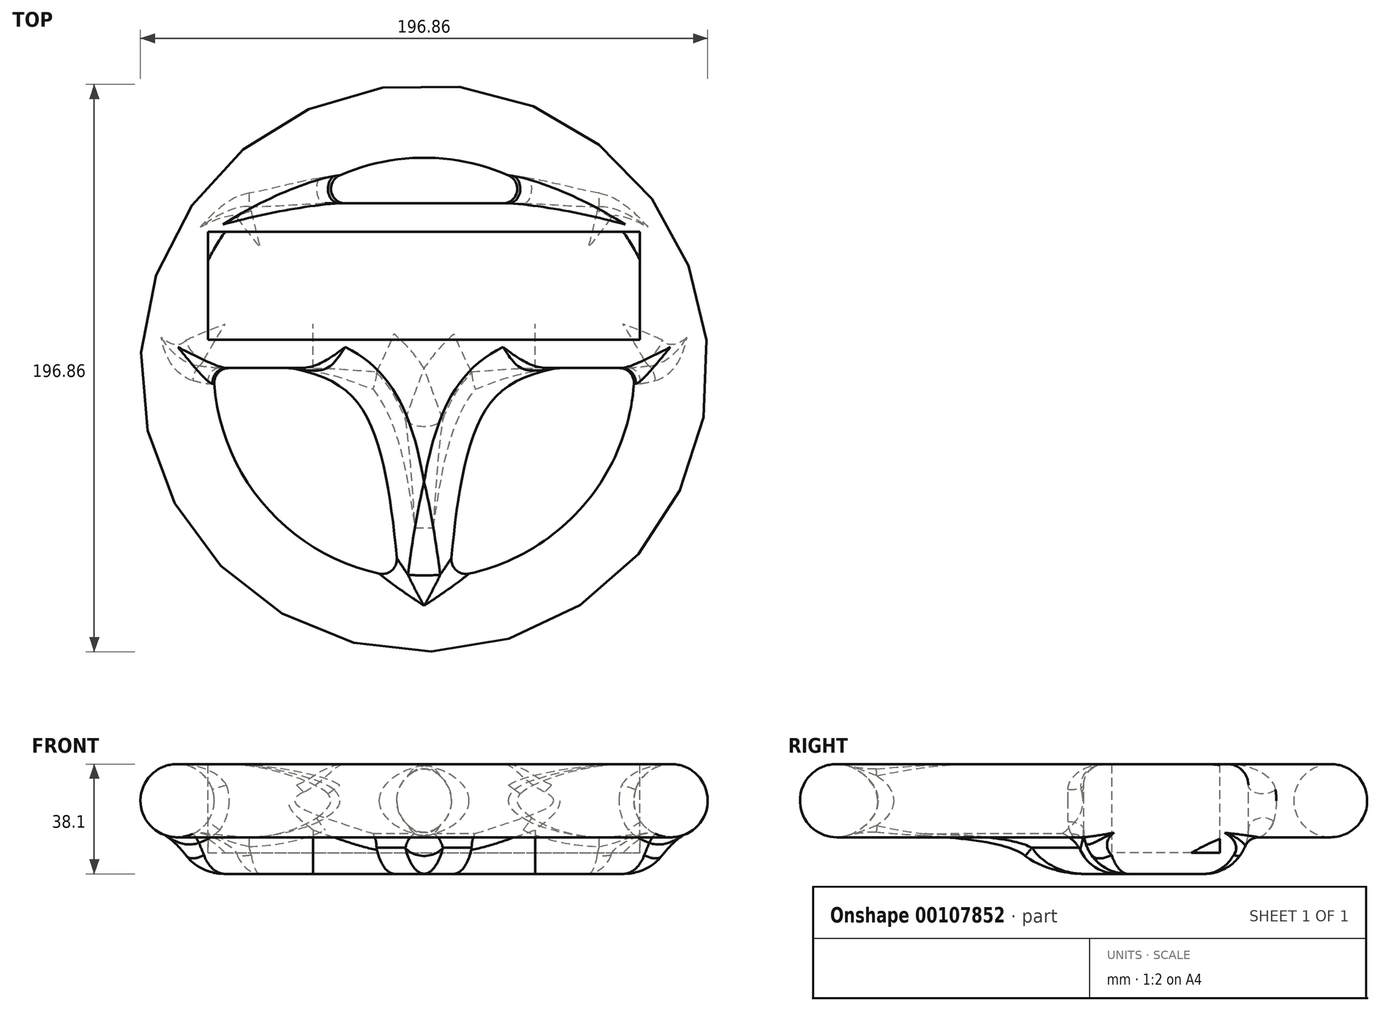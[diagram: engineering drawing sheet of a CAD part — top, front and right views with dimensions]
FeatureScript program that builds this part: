
annotation { "Feature Type Name" : "Feature", "Feature Type Description" : "" }
export const myFeature = defineFeature(function(context is Context, id is Id, definition is map)
    precondition{}
    {
        {
            var Q0;
            Q0=qCreatedBy(makeId("Top.planeOp"),FACE);
            var sketch = newSketch(context, id + "F0", { "sketchPlane" : qUnion([Q0])});
            skCircle(sketch, "E0", {"center": v(0, 0) * mm, "radius": 98.43 * mm});
            skArc(sketch, "E1", {"start": v(-73.03, 0) * mm, "mid": v(0, -73.03) * mm, "end": v(73.03, 0) * mm});
            skLineSegment(sketch, "E2", {"start": v(-45.46, 57.15) * mm, "end": v(45.46, 57.15) * mm});
            skLineSegment(sketch, "E3", {"start": v(73.03, 0) * mm, "end": v(-73.03, 0) * mm});
            skFitSpline(sketch, "E4", {"points": [v(-46.06, 0) * mm, v(-21.33, -14.47) * mm, v(-8.89, -72.48) * mm], "startDerivative": vector(87.72, -17.65) * mm, "endDerivative": vector(11.08, -128.98) * mm});
            skFitSpline(sketch, "E5.MirrorCS", {"points": [v(46.06, 0) * mm, v(21.33, -14.47) * mm, v(8.89, -72.48) * mm], "startDerivative": vector(-87.72, -17.65) * mm, "endDerivative": vector(-11.08, -128.98) * mm});
            skArc(sketch, "E6.trimOffspring", {"start": v(45.46, 57.15) * mm, "mid": v(0, 73.03) * mm, "end": v(-45.46, 57.15) * mm});
            skSolve(sketch);
        }
        {
            var Q0;
            Q0=makeQuery(id+"F0.imprint","IMPRINT",FACE,{"disambiguationData":[TD([[makeQuery(id+"F0.imprint","IMPRINT",EDGE,{"derivedFrom":sQuery(id+"F0.wireOp",EDGE,"E0")}),1.0]])]});
            var Q1;
            {var subQ0=sQuery(id+"F0.wireOp",EDGE,"E4");Q1=makeQuery(id+"F0.imprint","IMPRINT",FACE,{"disambiguationData":[TD([[makeQuery(id+"F0.imprint","IMPRINT",EDGE,{"derivedFrom":subQ0}),1.0]])]});}
            extrude(context, id + "F1", {"entities" : qUnion([Q0, Q1]), "depth" : 25.4 * mm});
        }
        {
            var Q0;
            Q0=makeQuery(id+"F1.opExtrude","CAP_EDGE",EDGE,{"disambiguationData":[OSD([sQuery(id+"F0.wireOp",EDGE,"E0")])],"isStart":false});
            var Q1;
            Q1=makeQuery(id+"F1.opExtrude","CAP_EDGE",EDGE,{"disambiguationData":[OSD([sQuery(id+"F0.wireOp",EDGE,"E0")])],"isStart":true});
            fillet(context, id + "F2", {"entities" : qUnion([Q0, Q1]), "radius" : 12.7 * mm, "tangentPropagation" : true, "allowEdgeOverflow" : false});
        }
        {
            var Q0;
            {var subQ0=sQuery(id+"F0.wireOp",EDGE,"E1");Q0=makeQuery(id+"F1.opExtrude","CAP_EDGE",EDGE,{"disambiguationData":[OSD([subQ0]),TDD([makeQuery(id+"F0.imprint","IMPRINT",EDGE,{"disambiguationData":[TD([[makeQuery(id+"F0.imprint","INTERSECT",VERTEX,{"disambiguationData":[OD(0.0)],"derivedFrom":[subQ0,sQuery(id+"F0.wireOp",EDGE,"E3")]}),-1.0]])],"derivedFrom":subQ0})])],"isStart":false});}
            var Q1;
            {var subQ0=sQuery(id+"F0.wireOp",EDGE,"E1");Q1=makeQuery(id+"F1.opExtrude","CAP_EDGE",EDGE,{"disambiguationData":[OSD([subQ0]),TDD([makeQuery(id+"F0.imprint","IMPRINT",EDGE,{"disambiguationData":[TD([[makeQuery(id+"F0.imprint","INTERSECT",VERTEX,{"disambiguationData":[OD(1.0)],"derivedFrom":[subQ0,sQuery(id+"F0.wireOp",EDGE,"E3")]}),1.0]])],"derivedFrom":subQ0})])],"isStart":false});}
            var Q2;
            Q2=makeQuery(id+"F1.opExtrude","CAP_EDGE",EDGE,{"disambiguationData":[OSD([sQuery(id+"F0.wireOp",EDGE,"E6.trimOffspring")])],"isStart":false});
            fillet(context, id + "F3", {"entities" : qUnion([Q0, Q1, Q2]), "radius" : 12.7 * mm, "tangentPropagation" : true, "allowEdgeOverflow" : false});
        }
        {
            var Q0;
            {var subQ0=sQuery(id+"F0.wireOp",EDGE,"E1");Q0=makeQuery(id+"F1.opExtrude","CAP_EDGE",EDGE,{"disambiguationData":[OSD([subQ0]),TDD([makeQuery(id+"F0.imprint","IMPRINT",EDGE,{"disambiguationData":[TD([[makeQuery(id+"F0.imprint","INTERSECT",VERTEX,{"disambiguationData":[OD(1.0)],"derivedFrom":[subQ0,sQuery(id+"F0.wireOp",EDGE,"E3")]}),1.0]])],"derivedFrom":subQ0})])],"isStart":true});}
            var Q1;
            Q1=makeQuery(id+"F1.opExtrude","CAP_EDGE",EDGE,{"disambiguationData":[OSD([sQuery(id+"F0.wireOp",EDGE,"E6.trimOffspring")])],"isStart":true});
            var Q2;
            {var subQ0=sQuery(id+"F0.wireOp",EDGE,"E1");Q2=makeQuery(id+"F1.opExtrude","CAP_EDGE",EDGE,{"disambiguationData":[OSD([subQ0]),TDD([makeQuery(id+"F0.imprint","IMPRINT",EDGE,{"disambiguationData":[TD([[makeQuery(id+"F0.imprint","INTERSECT",VERTEX,{"disambiguationData":[OD(0.0)],"derivedFrom":[subQ0,sQuery(id+"F0.wireOp",EDGE,"E3")]}),-1.0]])],"derivedFrom":subQ0})])],"isStart":true});}
            fillet(context, id + "F4", {"entities" : qUnion([Q0, Q1, Q2]), "radius" : 12.7 * mm, "tangentPropagation" : true, "allowEdgeOverflow" : false});
        }
        {
            var Q0;
            Q0=makeQuery(id+"F1.opExtrude","CAP_EDGE",EDGE,{"disambiguationData":[OSD([sQuery(id+"F0.wireOp",EDGE,"E5.MirrorCS")])],"isStart":false});
            var Q1;
            Q1=makeQuery(id+"F1.opExtrude","CAP_EDGE",EDGE,{"disambiguationData":[OSD([sQuery(id+"F0.wireOp",EDGE,"E4")])],"isStart":false});
            var Q2;
            Q2=makeQuery(id+"F1.opExtrude","CAP_EDGE",EDGE,{"disambiguationData":[OSD([sQuery(id+"F0.wireOp",EDGE,"E5.MirrorCS")])],"isStart":true});
            var Q3;
            Q3=makeQuery(id+"F1.opExtrude","CAP_EDGE",EDGE,{"disambiguationData":[OSD([sQuery(id+"F0.wireOp",EDGE,"E4")])],"isStart":true});
            fillet(context, id + "F5", {"entities" : qUnion([Q0, Q1, Q2, Q3]), "radius" : 12.7 * mm, "tangentPropagation" : true, "allowEdgeOverflow" : false});
        }
        {
            var Q0;
            {var subQ0=sQuery(id+"F0.wireOp",EDGE,"E3");Q0=makeQuery(id+"F1.opExtrude","CAP_EDGE",EDGE,{"disambiguationData":[OSD([subQ0]),TDD([makeQuery(id+"F0.imprint","IMPRINT",EDGE,{"disambiguationData":[TD([[makeQuery(id+"F0.imprint","INTERSECT",VERTEX,{"disambiguationData":[OD(1.0)],"derivedFrom":[sQuery(id+"F0.wireOp",EDGE,"E1"),subQ0]}),-1.0]])],"derivedFrom":subQ0})])],"isStart":false});}
            var Q1;
            {var subQ0=sQuery(id+"F0.wireOp",EDGE,"E3");Q1=makeQuery(id+"F1.opExtrude","CAP_EDGE",EDGE,{"disambiguationData":[OSD([subQ0]),TDD([makeQuery(id+"F0.imprint","IMPRINT",EDGE,{"disambiguationData":[TD([[makeQuery(id+"F0.imprint","INTERSECT",VERTEX,{"disambiguationData":[OD(0.0)],"derivedFrom":[sQuery(id+"F0.wireOp",EDGE,"E1"),subQ0]}),1.0]])],"derivedFrom":subQ0})])],"isStart":false});}
            var Q2;
            Q2=makeQuery(id+"F1.opExtrude","CAP_EDGE",EDGE,{"disambiguationData":[OSD([sQuery(id+"F0.wireOp",EDGE,"E2")])],"isStart":false});
            fillet(context, id + "F6", {"entities" : qUnion([Q0, Q1, Q2]), "radius" : 7.3 * mm, "tangentPropagation" : true, "allowEdgeOverflow" : false});
        }
        {
            var Q0;
            Q0=makeQuery(id+"F5.opFillet","BLEND_EDGE",EDGE,{"blendedFrom":[makeQuery(id+"F1.opExtrude","CAP_EDGE",EDGE,{"disambiguationData":[OSD([sQuery(id+"F0.wireOp",EDGE,"E5.MirrorCS")])],"isStart":false}),makeQuery(id+"F2.opFillet","BLEND_FACE",FACE,{"disambiguationData":[OSD([sQuery(id+"F0.wireOp",EDGE,"E0")])]})],"blendedInto":[makeQuery(id+"F2.opFillet","BLEND_FACE",FACE,{"disambiguationData":[OSD([sQuery(id+"F0.wireOp",EDGE,"E0")])]})]});
            var Q1;
            Q1=makeQuery(id+"F5.opFillet","BLEND_EDGE",EDGE,{"blendedFrom":[makeQuery(id+"F1.opExtrude","CAP_EDGE",EDGE,{"disambiguationData":[OSD([sQuery(id+"F0.wireOp",EDGE,"E4")])],"isStart":false}),makeQuery(id+"F2.opFillet","BLEND_FACE",FACE,{"disambiguationData":[OSD([sQuery(id+"F0.wireOp",EDGE,"E0")])]})],"blendedInto":[makeQuery(id+"F2.opFillet","BLEND_FACE",FACE,{"disambiguationData":[OSD([sQuery(id+"F0.wireOp",EDGE,"E0")])]})]});
            fillet(context, id + "F7", {"entities" : qUnion([Q0, Q1]), "radius" : 5.08 * mm, "tangentPropagation" : true, "allowEdgeOverflow" : false});
        }
        {
            var Q0;
            Q0=makeQuery(id+"F1.opExtrude","CAP_FACE",FACE,{"disambiguationData":[OSD([sQuery(id+"F0.wireOp",EDGE,"E0"),sQuery(id+"F0.wireOp",EDGE,"E1"),sQuery(id+"F0.wireOp",EDGE,"E2"),sQuery(id+"F0.wireOp",EDGE,"E3"),sQuery(id+"F0.wireOp",EDGE,"E4"),sQuery(id+"F0.wireOp",EDGE,"E5.MirrorCS"),sQuery(id+"F0.wireOp",EDGE,"E6.trimOffspring")])],"isStart":true});
            extrude(context, id + "F8", {"entities" : qUnion([Q0]), "operationType" : NewBodyOperationType.ADD, "depth" : 12.7 * mm});
        }
        {
            var Q0;
            {var subQ0=sQuery(id+"F0.wireOp",EDGE,"E6.trimOffspring");var subQ1=sQuery(id+"F0.wireOp",EDGE,"E5.MirrorCS");var subQ2=sQuery(id+"F0.wireOp",EDGE,"E4");var subQ3=sQuery(id+"F0.wireOp",EDGE,"E3");var subQ4=sQuery(id+"F0.wireOp",EDGE,"E2");var subQ5=sQuery(id+"F0.wireOp",EDGE,"E1");var subQ6=sQuery(id+"F0.wireOp",EDGE,"E0");var subQ7=makeQuery(id+"F5.opFillet","BLEND_EDGE",EDGE,{"blendedFrom":[makeQuery(id+"F1.opExtrude","CAP_EDGE",EDGE,{"disambiguationData":[OSD([subQ2])],"isStart":true}),makeQuery(id+"F1.opExtrude","CAP_FACE",FACE,{"disambiguationData":[OSD([subQ6,subQ5,subQ4,subQ3,subQ2,subQ1,subQ0])],"isStart":true})],"blendedInto":[makeQuery(id+"F1.opExtrude","CAP_FACE",FACE,{"disambiguationData":[OSD([subQ6,subQ5,subQ4,subQ3,subQ2,subQ1,subQ0])],"isStart":true})]});Q0=makeQuery(id+"F8.boolean.opBoolean","MERGE",EDGE,{"derivedFrom":[subQ7,makeQuery(id+"F8.opExtrude","CAP_EDGE",EDGE,{"disambiguationData":[OSD([subQ6,subQ5,subQ4,subQ3,subQ2,subQ1,subQ0]),TDD([subQ7])],"isStart":true})]});}
            var Q1;
            {var subQ0=sQuery(id+"F0.wireOp",EDGE,"E6.trimOffspring");var subQ1=sQuery(id+"F0.wireOp",EDGE,"E5.MirrorCS");var subQ2=sQuery(id+"F0.wireOp",EDGE,"E4");var subQ3=sQuery(id+"F0.wireOp",EDGE,"E3");var subQ4=sQuery(id+"F0.wireOp",EDGE,"E2");var subQ5=sQuery(id+"F0.wireOp",EDGE,"E1");var subQ6=sQuery(id+"F0.wireOp",EDGE,"E0");var subQ7=makeQuery(id+"F5.opFillet","BLEND_EDGE",EDGE,{"blendedFrom":[makeQuery(id+"F1.opExtrude","CAP_EDGE",EDGE,{"disambiguationData":[OSD([subQ1])],"isStart":true}),makeQuery(id+"F1.opExtrude","CAP_FACE",FACE,{"disambiguationData":[OSD([subQ6,subQ5,subQ4,subQ3,subQ2,subQ1,subQ0])],"isStart":true})],"blendedInto":[makeQuery(id+"F1.opExtrude","CAP_FACE",FACE,{"disambiguationData":[OSD([subQ6,subQ5,subQ4,subQ3,subQ2,subQ1,subQ0])],"isStart":true})]});Q1=makeQuery(id+"F8.boolean.opBoolean","MERGE",EDGE,{"derivedFrom":[subQ7,makeQuery(id+"F8.opExtrude","CAP_EDGE",EDGE,{"disambiguationData":[OSD([subQ6,subQ5,subQ4,subQ3,subQ2,subQ1,subQ0]),TDD([subQ7])],"isStart":true})]});}
            var Q2;
            {var subQ0=sQuery(id+"F0.wireOp",EDGE,"E3");var subQ1=sQuery(id+"F0.wireOp",EDGE,"E5.MirrorCS");Q2=makeQuery(id+"F5.opFillet","BLEND_EDGE",EDGE,{"blendedFrom":[makeQuery(id+"F1.opExtrude","CAP_EDGE",EDGE,{"disambiguationData":[OSD([subQ1])],"isStart":true}),makeQuery(id+"F1.opExtrude","SWEPT_FACE",FACE,{"disambiguationData":[OSD([subQ0]),TDD([makeQuery(id+"F0.imprint","IMPRINT",EDGE,{"disambiguationData":[TD([[makeQuery(id+"F0.imprint","INTERSECT",VERTEX,{"disambiguationData":[OD(1.0)],"derivedFrom":[sQuery(id+"F0.wireOp",EDGE,"E1"),subQ0]}),-1.0]])],"derivedFrom":subQ0})])]})],"blendedInto":[makeQuery(id+"F1.opExtrude","SWEPT_FACE",FACE,{"disambiguationData":[OSD([subQ0]),TDD([makeQuery(id+"F0.imprint","IMPRINT",EDGE,{"disambiguationData":[TD([[makeQuery(id+"F0.imprint","INTERSECT",VERTEX,{"disambiguationData":[OD(1.0)],"derivedFrom":[sQuery(id+"F0.wireOp",EDGE,"E1"),subQ0]}),-1.0]])],"derivedFrom":subQ0})])]})]});}
            var Q3;
            {var subQ0=sQuery(id+"F0.wireOp",EDGE,"E3");var subQ1=sQuery(id+"F0.wireOp",EDGE,"E4");Q3=makeQuery(id+"F5.opFillet","BLEND_EDGE",EDGE,{"blendedFrom":[makeQuery(id+"F1.opExtrude","CAP_EDGE",EDGE,{"disambiguationData":[OSD([subQ1])],"isStart":true}),makeQuery(id+"F1.opExtrude","SWEPT_FACE",FACE,{"disambiguationData":[OSD([subQ0]),TDD([makeQuery(id+"F0.imprint","IMPRINT",EDGE,{"disambiguationData":[TD([[makeQuery(id+"F0.imprint","INTERSECT",VERTEX,{"disambiguationData":[OD(0.0)],"derivedFrom":[sQuery(id+"F0.wireOp",EDGE,"E1"),subQ0]}),1.0]])],"derivedFrom":subQ0})])]})],"blendedInto":[makeQuery(id+"F1.opExtrude","SWEPT_FACE",FACE,{"disambiguationData":[OSD([subQ0]),TDD([makeQuery(id+"F0.imprint","IMPRINT",EDGE,{"disambiguationData":[TD([[makeQuery(id+"F0.imprint","INTERSECT",VERTEX,{"disambiguationData":[OD(0.0)],"derivedFrom":[sQuery(id+"F0.wireOp",EDGE,"E1"),subQ0]}),1.0]])],"derivedFrom":subQ0})])]})]});}
            fillet(context, id + "F9", {"entities" : qUnion([Q0, Q1, Q2, Q3]), "radius" : 10.16 * mm, "tangentPropagation" : true, "allowEdgeOverflow" : false});
        }
        {
            var Q0;
            Q0=makeQuery(id+"F8.opExtrude","CAP_FACE",FACE,{"disambiguationData":[OSD([sQuery(id+"F0.wireOp",EDGE,"E0"),sQuery(id+"F0.wireOp",EDGE,"E1"),sQuery(id+"F0.wireOp",EDGE,"E2"),sQuery(id+"F0.wireOp",EDGE,"E3"),sQuery(id+"F0.wireOp",EDGE,"E4"),sQuery(id+"F0.wireOp",EDGE,"E5.MirrorCS"),sQuery(id+"F0.wireOp",EDGE,"E6.trimOffspring")])],"isStart":false});
            fillet(context, id + "F10", {"entities" : qUnion([Q0]), "radius" : 15.24 * mm, "tangentPropagation" : true, "allowEdgeOverflow" : false});
        }
        {
            var Q0;
            {var subQ0=sQuery(id+"F0.wireOp",EDGE,"E0");var subQ1=sQuery(id+"F0.wireOp",EDGE,"E6.trimOffspring");var subQ2=sQuery(id+"F0.wireOp",EDGE,"E5.MirrorCS");var subQ3=sQuery(id+"F0.wireOp",EDGE,"E4");var subQ4=sQuery(id+"F0.wireOp",EDGE,"E3");var subQ5=sQuery(id+"F0.wireOp",EDGE,"E2");var subQ6=sQuery(id+"F0.wireOp",EDGE,"E1");Q0=makeQuery(id+"F10.opFillet","BLEND_EDGE",EDGE,{"blendedFrom":[makeQuery(id+"F8.opExtrude","CAP_EDGE",EDGE,{"disambiguationData":[OSD([subQ0,subQ6,subQ5,subQ4,subQ3,subQ2,subQ1]),TDD([makeQuery(id+"F2.opFillet","BLEND_EDGE",EDGE,{"blendedFrom":[makeQuery(id+"F1.opExtrude","CAP_EDGE",EDGE,{"disambiguationData":[OSD([subQ0])],"isStart":true}),makeQuery(id+"F1.opExtrude","CAP_FACE",FACE,{"disambiguationData":[OSD([subQ0,subQ6,subQ5,subQ4,subQ3,subQ2,subQ1])],"isStart":true})],"blendedInto":[makeQuery(id+"F1.opExtrude","CAP_FACE",FACE,{"disambiguationData":[OSD([subQ0,subQ6,subQ5,subQ4,subQ3,subQ2,subQ1])],"isStart":true})]})])],"isStart":false}),makeQuery(id+"F2.opFillet","BLEND_FACE",FACE,{"disambiguationData":[OSD([subQ0])]})],"blendedInto":[makeQuery(id+"F2.opFillet","BLEND_FACE",FACE,{"disambiguationData":[OSD([subQ0])]})]});}
            fillet(context, id + "F11", {"entities" : qUnion([Q0]), "radius" : 25.4 * mm, "tangentPropagation" : true, "allowEdgeOverflow" : false});
        }
        {
            var Q0;
            {var subQ0=sQuery(id+"F0.wireOp",EDGE,"E3");var subQ1=sQuery(id+"F0.wireOp",EDGE,"E1");var subQ2=sQuery(id+"F0.wireOp",EDGE,"E5.MirrorCS");var subQ3=sQuery(id+"F0.wireOp",EDGE,"E6.trimOffspring");var subQ4=sQuery(id+"F0.wireOp",EDGE,"E4");var subQ5=sQuery(id+"F0.wireOp",EDGE,"E2");var subQ6=sQuery(id+"F0.wireOp",EDGE,"E0");Q0=makeQuery(id+"F10.opFillet","BLEND_EDGE",EDGE,{"blendedFrom":[makeQuery(id+"F8.opExtrude","CAP_EDGE",EDGE,{"disambiguationData":[OSD([subQ6,subQ1,subQ5,subQ0,subQ4,subQ2,subQ3]),TDD([makeQuery(id+"F2.opFillet","BLEND_EDGE",EDGE,{"blendedFrom":[makeQuery(id+"F1.opExtrude","CAP_EDGE",EDGE,{"disambiguationData":[OSD([subQ6])],"isStart":true}),makeQuery(id+"F1.opExtrude","CAP_FACE",FACE,{"disambiguationData":[OSD([subQ6,subQ1,subQ5,subQ0,subQ4,subQ2,subQ3])],"isStart":true})],"blendedInto":[makeQuery(id+"F1.opExtrude","CAP_FACE",FACE,{"disambiguationData":[OSD([subQ6,subQ1,subQ5,subQ0,subQ4,subQ2,subQ3])],"isStart":true})]})])],"isStart":false}),makeQuery(id+"F8.opExtrude","CAP_EDGE",EDGE,{"disambiguationData":[OSD([subQ0]),TDD([makeQuery(id+"F1.opExtrude","CAP_EDGE",EDGE,{"disambiguationData":[OSD([subQ0]),TDD([makeQuery(id+"F0.imprint","IMPRINT",EDGE,{"disambiguationData":[TD([[makeQuery(id+"F0.imprint","INTERSECT",VERTEX,{"disambiguationData":[OD(1.0)],"derivedFrom":[subQ1,subQ0]}),-1.0]])],"derivedFrom":subQ0})])],"isStart":true})])],"isStart":false})],"blendedInto":[]});}
            var Q1;
            {var subQ0=sQuery(id+"F0.wireOp",EDGE,"E6.trimOffspring");var subQ1=sQuery(id+"F0.wireOp",EDGE,"E5.MirrorCS");var subQ2=sQuery(id+"F0.wireOp",EDGE,"E4");var subQ3=sQuery(id+"F0.wireOp",EDGE,"E3");var subQ4=sQuery(id+"F0.wireOp",EDGE,"E2");var subQ5=sQuery(id+"F0.wireOp",EDGE,"E1");var subQ6=sQuery(id+"F0.wireOp",EDGE,"E0");Q1=makeQuery(id+"F10.opFillet","BLEND_EDGE",EDGE,{"blendedFrom":[makeQuery(id+"F8.opExtrude","CAP_EDGE",EDGE,{"disambiguationData":[OSD([subQ4])],"isStart":false}),makeQuery(id+"F8.opExtrude","CAP_EDGE",EDGE,{"disambiguationData":[OSD([subQ6,subQ5,subQ4,subQ3,subQ2,subQ1,subQ0]),TDD([makeQuery(id+"F2.opFillet","BLEND_EDGE",EDGE,{"blendedFrom":[makeQuery(id+"F1.opExtrude","CAP_EDGE",EDGE,{"disambiguationData":[OSD([subQ6])],"isStart":true}),makeQuery(id+"F1.opExtrude","CAP_FACE",FACE,{"disambiguationData":[OSD([subQ6,subQ5,subQ4,subQ3,subQ2,subQ1,subQ0])],"isStart":true})],"blendedInto":[makeQuery(id+"F1.opExtrude","CAP_FACE",FACE,{"disambiguationData":[OSD([subQ6,subQ5,subQ4,subQ3,subQ2,subQ1,subQ0])],"isStart":true})]})])],"isStart":false})],"blendedInto":[]});}
            var Q2;
            {var subQ0=sQuery(id+"F0.wireOp",EDGE,"E3");var subQ1=sQuery(id+"F0.wireOp",EDGE,"E1");var subQ2=sQuery(id+"F0.wireOp",EDGE,"E4");var subQ3=sQuery(id+"F0.wireOp",EDGE,"E0");var subQ4=sQuery(id+"F0.wireOp",EDGE,"E6.trimOffspring");var subQ5=sQuery(id+"F0.wireOp",EDGE,"E5.MirrorCS");var subQ6=sQuery(id+"F0.wireOp",EDGE,"E2");Q2=makeQuery(id+"F11.opFillet","BLEND_EDGE",EDGE,{"blendedFrom":[makeQuery(id+"F10.opFillet","BLEND_EDGE",EDGE,{"blendedFrom":[makeQuery(id+"F8.opExtrude","CAP_EDGE",EDGE,{"disambiguationData":[OSD([subQ3,subQ1,subQ6,subQ0,subQ2,subQ5,subQ4]),TDD([makeQuery(id+"F2.opFillet","BLEND_EDGE",EDGE,{"blendedFrom":[makeQuery(id+"F1.opExtrude","CAP_EDGE",EDGE,{"disambiguationData":[OSD([subQ3])],"isStart":true}),makeQuery(id+"F1.opExtrude","CAP_FACE",FACE,{"disambiguationData":[OSD([subQ3,subQ1,subQ6,subQ0,subQ2,subQ5,subQ4])],"isStart":true})],"blendedInto":[makeQuery(id+"F1.opExtrude","CAP_FACE",FACE,{"disambiguationData":[OSD([subQ3,subQ1,subQ6,subQ0,subQ2,subQ5,subQ4])],"isStart":true})]})])],"isStart":false}),makeQuery(id+"F2.opFillet","BLEND_FACE",FACE,{"disambiguationData":[OSD([subQ3])]})],"blendedInto":[makeQuery(id+"F2.opFillet","BLEND_FACE",FACE,{"disambiguationData":[OSD([subQ3])]})]}),makeQuery(id+"F10.opFillet","BLEND_FACE",FACE,{"disambiguationData":[OSD([subQ0]),TDD([makeQuery(id+"F8.opExtrude","CAP_EDGE",EDGE,{"disambiguationData":[OSD([subQ0]),TDD([makeQuery(id+"F1.opExtrude","CAP_EDGE",EDGE,{"disambiguationData":[OSD([subQ0]),TDD([makeQuery(id+"F0.imprint","IMPRINT",EDGE,{"disambiguationData":[TD([[makeQuery(id+"F0.imprint","INTERSECT",VERTEX,{"disambiguationData":[OD(0.0)],"derivedFrom":[subQ1,subQ0]}),1.0]])],"derivedFrom":subQ0})])],"isStart":true})])],"isStart":false})]),OD(0.0)]})],"blendedInto":[makeQuery(id+"F10.opFillet","BLEND_FACE",FACE,{"disambiguationData":[OSD([subQ0]),TDD([makeQuery(id+"F8.opExtrude","CAP_EDGE",EDGE,{"disambiguationData":[OSD([subQ0]),TDD([makeQuery(id+"F1.opExtrude","CAP_EDGE",EDGE,{"disambiguationData":[OSD([subQ0]),TDD([makeQuery(id+"F0.imprint","IMPRINT",EDGE,{"disambiguationData":[TD([[makeQuery(id+"F0.imprint","INTERSECT",VERTEX,{"disambiguationData":[OD(0.0)],"derivedFrom":[subQ1,subQ0]}),1.0]])],"derivedFrom":subQ0})])],"isStart":true})])],"isStart":false})]),OD(0.0)]})]});}
            fillet(context, id + "F12", {"entities" : qUnion([Q0, Q1, Q2]), "radius" : 7.62 * mm, "tangentPropagation" : true, "allowEdgeOverflow" : false});
        }
        {
            var Q0;
            {var subQ0=sQuery(id+"F0.wireOp",EDGE,"E6.trimOffspring");var subQ1=sQuery(id+"F0.wireOp",EDGE,"E5.MirrorCS");var subQ2=sQuery(id+"F0.wireOp",EDGE,"E4");var subQ3=sQuery(id+"F0.wireOp",EDGE,"E3");var subQ4=sQuery(id+"F0.wireOp",EDGE,"E2");var subQ5=sQuery(id+"F0.wireOp",EDGE,"E1");var subQ6=sQuery(id+"F0.wireOp",EDGE,"E0");var subQ7=makeQuery(id+"F1.opExtrude","CAP_FACE",FACE,{"disambiguationData":[OSD([subQ6,subQ5,subQ4,subQ3,subQ2,subQ1,subQ0])],"isStart":true});Q0=makeQuery(id+"F10.opFillet","BLEND_EDGE",EDGE,{"blendedFrom":[makeQuery(id+"F8.opExtrude","CAP_EDGE",EDGE,{"disambiguationData":[OSD([subQ6,subQ5,subQ4,subQ3,subQ2,subQ1,subQ0]),TDD([makeQuery(id+"F5.opFillet","BLEND_EDGE",EDGE,{"blendedFrom":[makeQuery(id+"F1.opExtrude","CAP_EDGE",EDGE,{"disambiguationData":[OSD([subQ2])],"isStart":true}),subQ7],"blendedInto":[subQ7]})])],"isStart":false}),makeQuery(id+"F8.opExtrude","CAP_EDGE",EDGE,{"disambiguationData":[OSD([subQ6,subQ5,subQ4,subQ3,subQ2,subQ1,subQ0]),TDD([makeQuery(id+"F5.opFillet","BLEND_EDGE",EDGE,{"blendedFrom":[makeQuery(id+"F1.opExtrude","CAP_EDGE",EDGE,{"disambiguationData":[OSD([subQ1])],"isStart":true}),subQ7],"blendedInto":[subQ7]})])],"isStart":false})],"blendedInto":[]});}
            fillet(context, id + "F13", {"entities" : qUnion([Q0]), "radius" : 7.62 * mm, "tangentPropagation" : true, "allowEdgeOverflow" : false});
        }
        {
            var Q0;
            Q0=makeQuery(id+"F6.opFillet","BLEND_EDGE",EDGE,{"disambiguationData":[OD(1.0)],"blendedFrom":[makeQuery(id+"F1.opExtrude","CAP_EDGE",EDGE,{"disambiguationData":[OSD([sQuery(id+"F0.wireOp",EDGE,"E2")])],"isStart":false}),makeQuery(id+"F2.opFillet","BLEND_FACE",FACE,{"disambiguationData":[OSD([sQuery(id+"F0.wireOp",EDGE,"E0")])]})],"blendedInto":[makeQuery(id+"F2.opFillet","BLEND_FACE",FACE,{"disambiguationData":[OSD([sQuery(id+"F0.wireOp",EDGE,"E0")])]})]});
            var Q1;
            {var subQ0=sQuery(id+"F0.wireOp",EDGE,"E3");Q1=makeQuery(id+"F6.opFillet","BLEND_EDGE",EDGE,{"blendedFrom":[makeQuery(id+"F1.opExtrude","CAP_EDGE",EDGE,{"disambiguationData":[OSD([subQ0]),TDD([makeQuery(id+"F0.imprint","IMPRINT",EDGE,{"disambiguationData":[TD([[makeQuery(id+"F0.imprint","INTERSECT",VERTEX,{"disambiguationData":[OD(0.0)],"derivedFrom":[sQuery(id+"F0.wireOp",EDGE,"E1"),subQ0]}),1.0]])],"derivedFrom":subQ0})])],"isStart":false}),makeQuery(id+"F2.opFillet","BLEND_FACE",FACE,{"disambiguationData":[OSD([sQuery(id+"F0.wireOp",EDGE,"E0")])]})],"blendedInto":[makeQuery(id+"F2.opFillet","BLEND_FACE",FACE,{"disambiguationData":[OSD([sQuery(id+"F0.wireOp",EDGE,"E0")])]})]});}
            var Q2;
            {var subQ0=sQuery(id+"F0.wireOp",EDGE,"E3");Q2=makeQuery(id+"F6.opFillet","BLEND_EDGE",EDGE,{"blendedFrom":[makeQuery(id+"F1.opExtrude","CAP_EDGE",EDGE,{"disambiguationData":[OSD([subQ0]),TDD([makeQuery(id+"F0.imprint","IMPRINT",EDGE,{"disambiguationData":[TD([[makeQuery(id+"F0.imprint","INTERSECT",VERTEX,{"disambiguationData":[OD(1.0)],"derivedFrom":[sQuery(id+"F0.wireOp",EDGE,"E1"),subQ0]}),-1.0]])],"derivedFrom":subQ0})])],"isStart":false}),makeQuery(id+"F2.opFillet","BLEND_FACE",FACE,{"disambiguationData":[OSD([sQuery(id+"F0.wireOp",EDGE,"E0")])]})],"blendedInto":[makeQuery(id+"F2.opFillet","BLEND_FACE",FACE,{"disambiguationData":[OSD([sQuery(id+"F0.wireOp",EDGE,"E0")])]})]});}
            var Q3;
            Q3=makeQuery(id+"F6.opFillet","BLEND_EDGE",EDGE,{"disambiguationData":[OD(0.0)],"blendedFrom":[makeQuery(id+"F1.opExtrude","CAP_EDGE",EDGE,{"disambiguationData":[OSD([sQuery(id+"F0.wireOp",EDGE,"E2")])],"isStart":false}),makeQuery(id+"F2.opFillet","BLEND_FACE",FACE,{"disambiguationData":[OSD([sQuery(id+"F0.wireOp",EDGE,"E0")])]})],"blendedInto":[makeQuery(id+"F2.opFillet","BLEND_FACE",FACE,{"disambiguationData":[OSD([sQuery(id+"F0.wireOp",EDGE,"E0")])]})]});
            fillet(context, id + "F14", {"entities" : qUnion([Q0, Q1, Q2, Q3]), "radius" : 5.08 * mm, "tangentPropagation" : true, "allowEdgeOverflow" : false});
        }
        {
            var Q0;
            Q0=makeQuery(id+"F5.opFillet","BLEND_EDGE",EDGE,{"blendedFrom":[makeQuery(id+"F1.opExtrude","CAP_EDGE",EDGE,{"disambiguationData":[OSD([sQuery(id+"F0.wireOp",EDGE,"E4")])],"isStart":false}),makeQuery(id+"F1.opExtrude","CAP_EDGE",EDGE,{"disambiguationData":[OSD([sQuery(id+"F0.wireOp",EDGE,"E5.MirrorCS")])],"isStart":false})],"blendedInto":[]});
            fillet(context, id + "F15", {"entities" : qUnion([Q0]), "radius" : 7.62 * mm, "tangentPropagation" : true, "allowEdgeOverflow" : false});
        }
        {
            var Q0;
            Q0=makeQuery(id+"F1.opExtrude","CAP_FACE",FACE,{"disambiguationData":[OSD([sQuery(id+"F0.wireOp",EDGE,"E0"),sQuery(id+"F0.wireOp",EDGE,"E1"),sQuery(id+"F0.wireOp",EDGE,"E2"),sQuery(id+"F0.wireOp",EDGE,"E3"),sQuery(id+"F0.wireOp",EDGE,"E4"),sQuery(id+"F0.wireOp",EDGE,"E5.MirrorCS"),sQuery(id+"F0.wireOp",EDGE,"E6.trimOffspring")])],"isStart":false});
            var sketch = newSketch(context, id + "F16", { "sketchPlane" : qUnion([Q0])});
            skLineSegment(sketch, "E7.bottom", {"start": v(-74.93, 47.3) * mm, "end": v(74.93, 47.3) * mm});
            skLineSegment(sketch, "E7.top", {"start": v(-74.93, 9.84) * mm, "end": v(74.93, 9.84) * mm});
            skLineSegment(sketch, "E7.left", {"start": v(-74.93, 47.3) * mm, "end": v(-74.93, 9.84) * mm});
            skLineSegment(sketch, "E7.right", {"start": v(74.93, 47.3) * mm, "end": v(74.93, 9.84) * mm});
            skSolve(sketch);
        }
        {
            var Q0;
            {var subQ1=sQuery(id+"F16.wireOp",EDGE,"E7.top");Q0=makeQuery(id+"F16.imprint","IMPRINT",FACE,{"disambiguationData":[TD([[makeQuery(id+"F16.imprint","IMPRINT",EDGE,{"derivedFrom":subQ1}),1.0]])]});}
            var Q1;
            {var subQ0=sQuery(id+"F16.wireOp",EDGE,"E7.left");var subQ1=sQuery(id+"F16.wireOp",EDGE,"E7.bottom");var subQ2=makeQuery(id+"F16.imprint","INTERSECT",VERTEX,{"derivedFrom":[subQ1,subQ0]});Q1=makeQuery(id+"F16.imprint","IMPRINT",FACE,{"disambiguationData":[TD([[makeQuery(id+"F16.imprint","IMPRINT",EDGE,{"disambiguationData":[TD([[subQ2,-1.0]])],"derivedFrom":subQ1}),-1.0]])]});}
            var Q2;
            {var subQ0=sQuery(id+"F16.wireOp",EDGE,"E7.right");var subQ1=sQuery(id+"F16.wireOp",EDGE,"E7.bottom");var subQ2=makeQuery(id+"F16.imprint","INTERSECT",VERTEX,{"derivedFrom":[subQ1,subQ0]});Q2=makeQuery(id+"F16.imprint","IMPRINT",FACE,{"disambiguationData":[TD([[makeQuery(id+"F16.imprint","IMPRINT",EDGE,{"disambiguationData":[TD([[subQ2,1.0]])],"derivedFrom":subQ1}),-1.0]])]});}
            extrude(context, id + "F17", {"entities" : qUnion([Q0, Q1, Q2]), "operationType" : NewBodyOperationType.REMOVE, "oppositeDirection" : true, "depth" : 25.4 * mm});
        }
        {
            var Q0;
            Q0=makeQuery(id+"F17.boolean.opBoolean","COPY",FACE,{"derivedFrom":makeQuery(id+"F17.opExtrude","CAP_FACE",FACE,{"disambiguationData":[OSD([sQuery(id+"F16.wireOp",EDGE,"E7.bottom"),sQuery(id+"F16.wireOp",EDGE,"E7.top"),sQuery(id+"F16.wireOp",EDGE,"E7.left"),sQuery(id+"F16.wireOp",EDGE,"E7.right")])],"isStart":false})});
            extrude(context, id + "F18", {"entities" : qUnion([Q0]), "operationType" : NewBodyOperationType.REMOVE, "oppositeDirection" : true, "depth" : 5.38 * mm});
        }
    });
